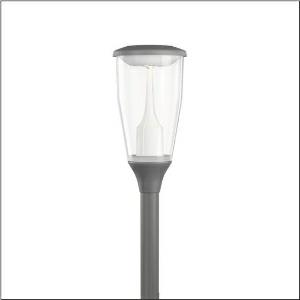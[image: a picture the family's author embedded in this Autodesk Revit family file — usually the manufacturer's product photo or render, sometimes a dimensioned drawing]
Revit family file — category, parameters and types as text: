
# Revit family: dl_11_iq___p1_0a_5xa5575ff14h000022_b904
name_source: partatom
category: Lighting Fixtures
units: mm (PartAtom-declared; Revit-internal decimal feet)

## family parameters
Cut with Voids When Loaded = No
Host = Face
Light Source = No
Part Type = Normal
Room Calculation Point = No
Round Connector Dimension = Use Diameter
Shared = No

## types (1)
- --- (1 x LED, 1530 lm, 10.5 W, 3000K)
    Apparent Load = 11 VA
    CIE Flux Codes = 34 63 91 95 100
    Color Rendering = 70
    Color Temperature = 3000K
    Default Elevation = 1800 mm
    Description = DL 11 iQ, mast luminaire, Module 540 iQ-SR, primary light control with 3 zone facetted reflector, of plastic, silver coated, highly specular, structured, primary optical cover: cover, of PMMA, transparent, light distribution: P1.0a, light emission: direct distribution, primary light characteristic: asymmetric, installation type: post-top, LED, High Power LED, rated luminous flux: 1.560lm, luminous efficacy: 149lm/W, light colour: 730, colour temperature: 3000K, control gear: iQ Street-Remote, control: Street-Remote, Auto-Match, Temp-Guard, Lumen-Switch, Night-Set, Smart-Wire, Light-Fading, Desk-Remote (wireless, voltage-free reading and setting of iQ features in the workshop via application-optimized NFC function/RFID function), optimised constant luminous flux control (CLO 2.0), mains connection: 220..240V, AC, 50/60Hz, connection cable pre-assembled, cable length: 5,5m, wiring characteristics: H07RN-F, 5-core, 1.5mm², start of lifetime: 10W, end of service life: 11W, reduction: 5W, luminaire housing, upper part, of diecast aluminium, coated, Siteco® metallic grey (DB 702S), spigot size: 76mm (post-top), mounting height: 3..5m, post-top mast mounting element, of diecast aluminium, coated, Siteco® metallic grey (DB 702S), Module 540 iQ-SR, traffic white (RAL 9016), equipment: standard, protection rating (complete): IP66, insulation class (complete): insulation class II (safety insulation), certification: CE, ENEC, ENEC+, VDE, impact resistance: IK07, packaging unit: 1 piece

Light Distribution: P1.0a
    Height = 665 mm
    Lamp = 1 x LED
    Lamp Light Flux = 1530 lm
    Lamp Power = 10.5 W
    Lamp count = 1
    Length = 334 mm
    Luminous efficacy = 146 lm/W
    Manufacturer = Siteco
    ModVariant = No
    Model = 5XA5575FF14H000022
    Number of Poles = 1
    OnlyDefault = Yes
    Power Factor = 1
    Product Name = DL 11 iQ | P1.0a
    Product group = mast luminaire | pylon top
    ProductGroupID = 6100
    Protection Class = Protection class II
    Protection Degree = IP 66
    RLX_Detail_Level = 1
    RLX_Emergency_Light_Flux = 0 lm
    RLX_Emergency_Type = 0
    RLX_Emergency_Type_DB = No
    RlxData = <blob elided: 104729 chars, md5=63cc4931>
    Socket = socket
    Standby Power = 0 W
    System Light Flux = 1530 lm
    System Power = 11 W
    Type Comments = factory setting: luminous flux: 100 % | dim-lin: 254 | 419 mA
    Type Image = l_1258354.jpg
    URL = http://relux.com
    VarID = @adj_113281
    Voltage = 0 V
    Weight = 0.00 kg
    Width = 0 mm  [stored 0 ft]

note: [stored X ft] marks values corroborated as IEEE doubles in the binary element streams (Revit-internal decimal feet)

## geometry (parser evidence)
native form markers: Blend x4, Sweep x10
no freeform markers — native parametric forms only
